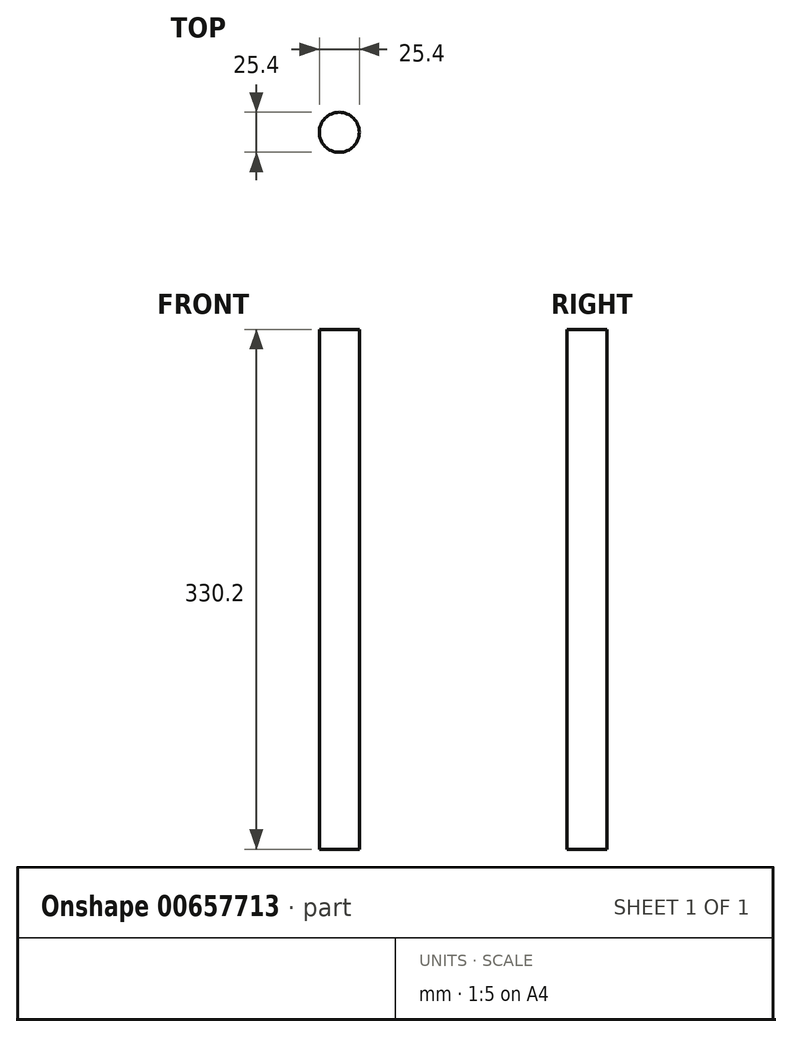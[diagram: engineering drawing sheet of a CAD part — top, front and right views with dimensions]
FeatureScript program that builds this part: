
annotation { "Feature Type Name" : "Feature", "Feature Type Description" : "" }
export const myFeature = defineFeature(function(context is Context, id is Id, definition is map)
    precondition{}
    {
        {
            var Q0;
            Q0=qCreatedBy(makeId("Top.planeOp"),FACE);
            var sketch = newSketch(context, id + "F0", { "sketchPlane" : qUnion([Q0])});
            skCircle(sketch, "E0", {"center": v(0, 0) * mm, "radius": 12.7 * mm});
            skSolve(sketch);
        }
        {
            var Q0;
            Q0=makeQuery(id+"F0.imprint","IMPRINT",FACE,{"disambiguationData":[TD([[makeQuery(id+"F0.imprint","IMPRINT",EDGE,{"derivedFrom":sQuery(id+"F0.wireOp",EDGE,"E0")}),1.0]])]});
            extrude(context, id + "F1", {"entities" : qUnion([Q0]), "depth" : 330.2 * mm, "offsetDistance" : 25.4 * mm});
        }
    });
